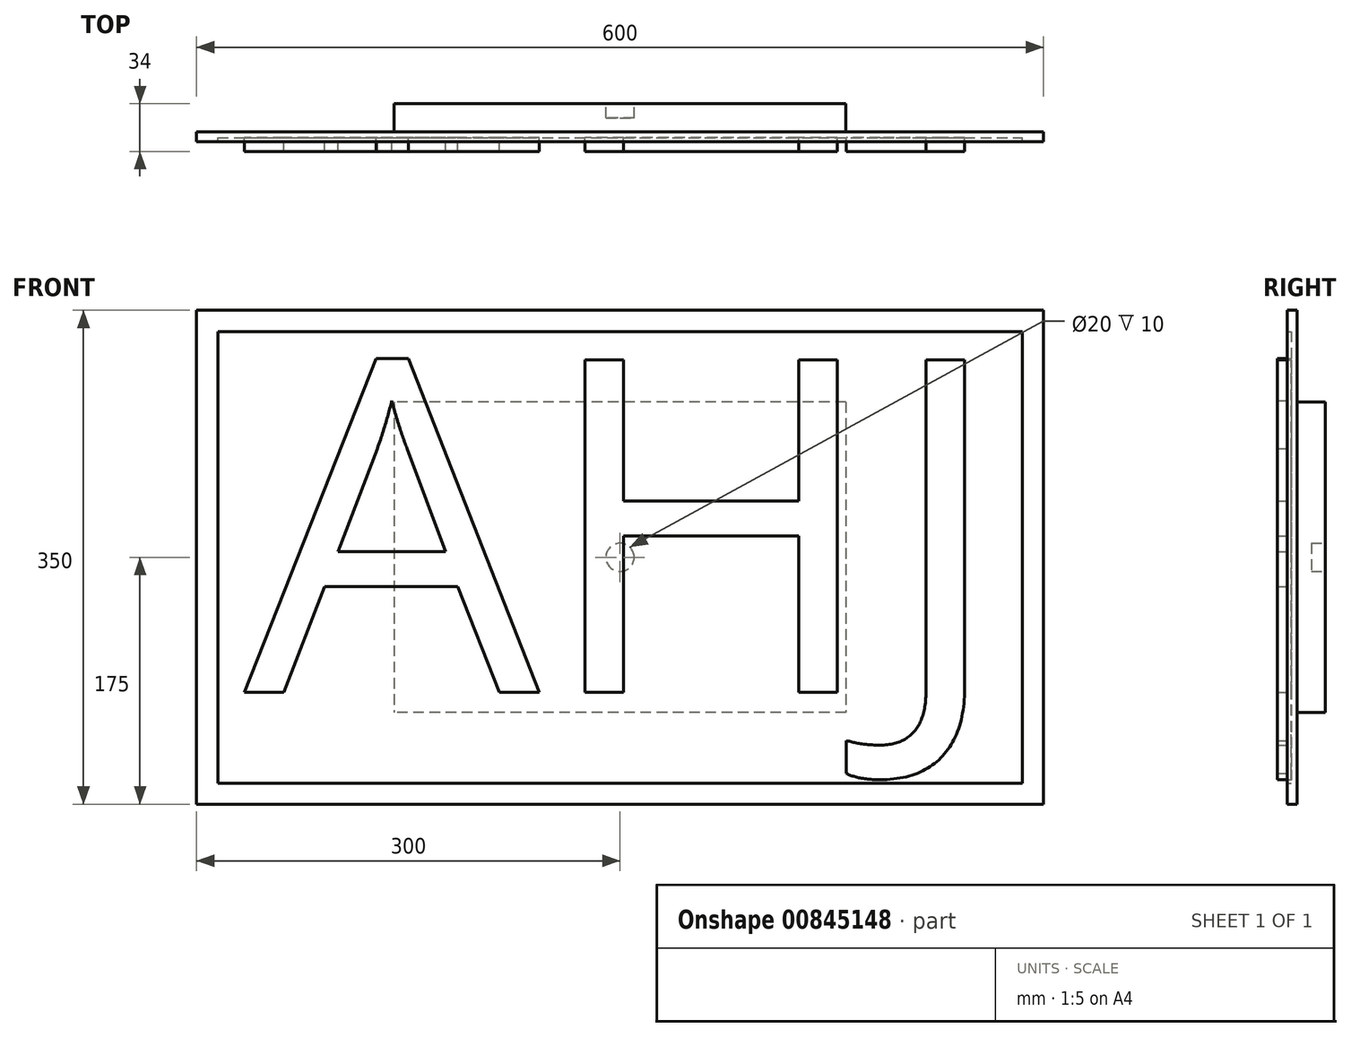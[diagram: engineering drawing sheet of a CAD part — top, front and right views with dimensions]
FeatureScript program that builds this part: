
annotation { "Feature Type Name" : "Feature", "Feature Type Description" : "" }
export const myFeature = defineFeature(function(context is Context, id is Id, definition is map)
    precondition{}
    {
        {
            var Q0;
            Q0=qCreatedBy(makeId("Front.planeOp"),FACE);
            var sketch = newSketch(context, id + "F0", { "sketchPlane" : qUnion([Q0])});
            skLineSegment(sketch, "E0.bottom", {"start": v(-300, 175) * mm, "end": v(300, 175) * mm});
            skLineSegment(sketch, "E0.top", {"start": v(-300, -175) * mm, "end": v(300, -175) * mm});
            skLineSegment(sketch, "E0.left", {"start": v(-300, 175) * mm, "end": v(-300, -175) * mm});
            skLineSegment(sketch, "E0.right", {"start": v(300, 175) * mm, "end": v(300, -175) * mm});
            skLineSegment(sketch, "E1.bottom", {"start": v(-285, 160) * mm, "end": v(285, 160) * mm});
            skLineSegment(sketch, "E1.top", {"start": v(-285, -160) * mm, "end": v(285, -160) * mm});
            skLineSegment(sketch, "E1.left", {"start": v(-285, 160) * mm, "end": v(-285, -160) * mm});
            skLineSegment(sketch, "E1.right", {"start": v(285, 160) * mm, "end": v(285, -160) * mm});
            skSolve(sketch);
        }
        {
            var Q0;
            Q0=makeQuery(id+"F0.imprint","IMPRINT",FACE,{"disambiguationData":[TD([[makeQuery(id+"F0.imprint","IMPRINT",EDGE,{"derivedFrom":sQuery(id+"F0.wireOp",EDGE,"E0.bottom")}),-1.0]])]});
            extrude(context, id + "F1", {"entities" : qUnion([Q0]), "depth" : 7 * mm, "offsetDistance" : 25 * mm});
        }
        {
            var Q0;
            Q0=makeQuery(id+"F0.imprint","IMPRINT",FACE,{"disambiguationData":[TD([[makeQuery(id+"F0.imprint","IMPRINT",EDGE,{"derivedFrom":sQuery(id+"F0.wireOp",EDGE,"E1.bottom")}),-1.0]])]});
            extrude(context, id + "F2", {"entities" : qUnion([Q0]), "operationType" : NewBodyOperationType.ADD, "depth" : 4 * mm, "offsetDistance" : 25 * mm});
        }
        {
            var Q0;
            Q0=makeQuery(id+"F0.imprint","IMPRINT",FACE,{"disambiguationData":[TD([[makeQuery(id+"F0.imprint","IMPRINT",EDGE,{"derivedFrom":sQuery(id+"F0.wireOp",EDGE,"E1.bottom")}),-1.0]])]});
            var sketch = newSketch(context, id + "F3", { "sketchPlane" : qUnion([Q0])});
            skLineSegment(sketch, "E2.bottom", {"start": v(160, 110) * mm, "end": v(-160, 110) * mm});
            skLineSegment(sketch, "E2.top", {"start": v(160, -110) * mm, "end": v(-160, -110) * mm});
            skLineSegment(sketch, "E2.left", {"start": v(160, 110) * mm, "end": v(160, -110) * mm});
            skLineSegment(sketch, "E2.right", {"start": v(-160, 110) * mm, "end": v(-160, -110) * mm});
            skSolve(sketch);
        }
        {
            var Q0;
            Q0 = qSketchRegion(id + "F3", true);
            extrude(context, id + "F4", {"entities" : qUnion([Q0]), "operationType" : NewBodyOperationType.ADD, "oppositeDirection" : true, "depth" : 20 * mm, "offsetDistance" : 25 * mm});
        }
        {
            var Q0;
            Q0=makeQuery(id+"F4.opExtrude","CAP_FACE",FACE,{"disambiguationData":[OSD([sQuery(id+"F3.wireOp",EDGE,"E2.bottom"),sQuery(id+"F3.wireOp",EDGE,"E2.top"),sQuery(id+"F3.wireOp",EDGE,"E2.left"),sQuery(id+"F3.wireOp",EDGE,"E2.right")])],"isStart":false});
            var sketch = newSketch(context, id + "F5", { "sketchPlane" : qUnion([Q0])});
            skCircle(sketch, "E3", {"center": v(0, 0) * mm, "radius": 10 * mm});
            skSolve(sketch);
        }
        {
            var Q0;
            Q0=makeQuery(id+"F5.imprint","IMPRINT",FACE,{"disambiguationData":[TD([[makeQuery(id+"F5.imprint","IMPRINT",EDGE,{"derivedFrom":sQuery(id+"F5.wireOp",EDGE,"E3")}),1.0]])]});
            extrude(context, id + "F6", {"entities" : qUnion([Q0]), "operationType" : NewBodyOperationType.REMOVE, "oppositeDirection" : true, "depth" : 10 * mm, "offsetDistance" : 25 * mm});
        }
        {
            var Q0;
            Q0=makeQuery(id+"F2.opExtrude","CAP_FACE",FACE,{"disambiguationData":[OSD([sQuery(id+"F0.wireOp",EDGE,"E1.bottom"),sQuery(id+"F0.wireOp",EDGE,"E1.top"),sQuery(id+"F0.wireOp",EDGE,"E1.left"),sQuery(id+"F0.wireOp",EDGE,"E1.right")])],"isStart":false});
            var sketch = newSketch(context, id + "F7", { "sketchPlane" : qUnion([Q0])});
            skText(sketch, "E4", { "text": "AHJ", "fontName": "OpenSans-Regular.ttf"});
            const initialGuessF7  = {"E4": [-0.26603, -0.09557, 1, 0, 0.23751]};
            skSetInitialGuess(sketch, initialGuessF7);
            skSolve(sketch);
        }
        {
            var Q0;
            Q0=makeQuery(id+"F7.imprint","IMPRINT",FACE,{"disambiguationData":[TD([[makeQuery(id+"F7.imprint","IMPRINT",EDGE,{"derivedFrom":sQuery(id+"F7.wireOp",EDGE,"E4.sketch_text.stroke-0")}),-1.0]])]});
            var Q1;
            Q1=makeQuery(id+"F7.imprint","IMPRINT",FACE,{"disambiguationData":[TD([[makeQuery(id+"F7.imprint","IMPRINT",EDGE,{"derivedFrom":sQuery(id+"F7.wireOp",EDGE,"E4.sketch_text.stroke-13")}),-1.0]])]});
            var Q2;
            Q2=makeQuery(id+"F7.imprint","IMPRINT",FACE,{"disambiguationData":[TD([[makeQuery(id+"F7.imprint","IMPRINT",EDGE,{"derivedFrom":sQuery(id+"F7.wireOp",EDGE,"E4.sketch_text.stroke-25")}),-1.0]])]});
            extrude(context, id + "F8", {"entities" : qUnion([Q0, Q1, Q2]), "operationType" : NewBodyOperationType.ADD, "depth" : 10 * mm, "offsetDistance" : 25 * mm});
        }
    });
